# Revit family: 603-A-4100-DN350
name_source: partatom
category: Pipe Accessories
units: mm (PartAtom-declared; Revit-internal decimal feet)

## family parameters
Always vertical = Yes
Cut with Voids When Loaded = No
Part Type = Valve - Breaks Into
Round Connector Dimension = Use Diameter
Shared = No
Work Plane-Based = No

## types (6) — shared parameters
Bolt_width = 20 mm  [stored 0.0656168 ft]
Bottm_cut = 216 mm  [stored 0.708661 ft]
Bottom_Flange_Thickness = 16 mm  [stored 0.0524934 ft]
D2 = 195 mm  [stored 0.639764 ft]
DN350_352 - 378 = 603-378-002-4100
DN350_352 -378 = 603-378-000-4100
DN350_372 - 396 = 603-396-002-4100
DN350_372 -396 = 603-396-000-4100
DN350_384 - 410 = 603-410-000-4100
DN350_384 -410 = 603-410-002-4100
Description_ = AVK UNIVERSAL SUPA® STRAIGHT COUPLING
H1 = 36 mm  [stored 0.11811 ft]
ID = 175 mm  [stored 0.574147 ft]
Nomianal_Diameter(DN) = 350 mm  [stored 1.14829 ft]
Nut = 10 mm  [stored 0.0328084 ft]
Rib_Thickness = 5 mm  [stored 0.0164042 ft]
Rib_length = 32 mm  [stored 0.104987 ft]
Rib_width = 499 mm  [stored 1.63714 ft]
Search_table = 603-A-4100-DN350
URL_product_pages = https://www.avkvalves.com

## per-type parameters (varying)
| type | Bolt_Ref | Bolt_Ref_2 | D | D3 | D4 | L | L1 | L2 | L3 | L_Ref | PCD | Washer_Ref | Washer_Ref_2 |
| 603-378-000-4100_DN350_352 - 378 | 158 mm | 148 mm  [stored 0.485564 ft] | 260 mm  [stored 0.853018 ft] | 210 mm  [stored 0.688976 ft] | 241 mm  [stored 0.790682 ft] | 186 mm  [stored 0.610236 ft] | 61 mm  [stored 0.200131 ft] | 170 mm  [stored 0.557743 ft] | 103 mm | 170 mm  [stored 0.557743 ft] | 450 mm  [stored 1.47638 ft] | 148 mm  [stored 0.485564 ft] | 145 mm  [stored 0.475722 ft] |
| 603-396-000-4100_DN350_372 - 396 | 200 mm  [stored 0.656168 ft] | 190 mm | 248 mm  [stored 0.813648 ft] | 202 mm | 241 mm  [stored 0.790682 ft] | 226 mm  [stored 0.74147 ft] | 62 mm  [stored 0.203412 ft] | 210 mm  [stored 0.688976 ft] | 145 mm  [stored 0.475722 ft] | 210 mm  [stored 0.688976 ft] | 450 mm  [stored 1.47638 ft] | 190 mm | 187 mm  [stored 0.613517 ft] |
| 603-410-002-4100_DN350_384 - 410 | 200 mm  [stored 0.656168 ft] | 190 mm | 264 mm  [stored 0.866142 ft] | 202 mm | 233 mm | 226 mm  [stored 0.74147 ft] | 62 mm  [stored 0.203412 ft] | 210 mm  [stored 0.688976 ft] | 145 mm  [stored 0.475722 ft] | 210 mm  [stored 0.688976 ft] | 435 mm | 190 mm | 187 mm  [stored 0.613517 ft] |
| 603-378-002-4100_DN350_352 - 378 | 158 mm | 148 mm  [stored 0.485564 ft] | 264 mm  [stored 0.866142 ft] | 210 mm  [stored 0.688976 ft] | 241 mm  [stored 0.790682 ft] | 186 mm  [stored 0.610236 ft] | 61 mm  [stored 0.200131 ft] | 170 mm  [stored 0.557743 ft] | 103 mm | 170 mm  [stored 0.557743 ft] | 450 mm  [stored 1.47638 ft] | 148 mm  [stored 0.485564 ft] | 145 mm  [stored 0.475722 ft] |
| 603-396-002-4100_DN350_372 - 396 | 200 mm  [stored 0.656168 ft] | 190 mm | 264 mm  [stored 0.866142 ft] | 202 mm | 241 mm  [stored 0.790682 ft] | 226 mm  [stored 0.74147 ft] | 62 mm  [stored 0.203412 ft] | 210 mm  [stored 0.688976 ft] | 145 mm  [stored 0.475722 ft] | 210 mm  [stored 0.688976 ft] | 450 mm  [stored 1.47638 ft] | 190 mm | 187 mm  [stored 0.613517 ft] |
| 603-410-000-4100_DN350_384 - 410 | 200 mm  [stored 0.656168 ft] | 190 mm | 260 mm  [stored 0.853018 ft] | 202 mm | 241 mm  [stored 0.790682 ft] | 226 mm  [stored 0.74147 ft] | 62 mm  [stored 0.203412 ft] | 210 mm  [stored 0.688976 ft] | 145 mm  [stored 0.475722 ft] | 210 mm  [stored 0.688976 ft] | 450 mm  [stored 1.47638 ft] | 190 mm | 187 mm  [stored 0.613517 ft] |

note: [stored X ft] marks values corroborated as IEEE doubles in the binary element streams (Revit-internal decimal feet)

## geometry (parser evidence)
native form markers: Sweep x6
no freeform markers — native parametric forms only
